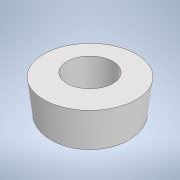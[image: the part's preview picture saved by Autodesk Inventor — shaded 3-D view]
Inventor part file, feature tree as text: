
AUTODESK INVENTOR PART (.ipt)
format: ipt  version: 2020.3 (Build 243373000, 373)  size: 97,280 bytes
history: native  units: mm
features: other x1, extrude x1, sketch x1
ambient origin geometry x8: Origin, YZ Plane, XZ Plane, XY Plane, X Axis, Y Axis, Z Axis, Center Point
bodies: Body1 (feature_tree)
feature tree (3):
  other  "ソリッド1"
  extrude  "押し出し1"  Depth=8.0mm
  sketch  "スケッチ1"
